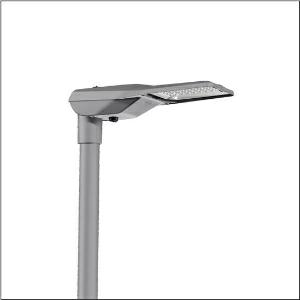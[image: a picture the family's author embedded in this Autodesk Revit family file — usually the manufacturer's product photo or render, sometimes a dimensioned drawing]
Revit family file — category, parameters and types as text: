
# Revit family: streetlight_sl_21_iq_mini___pl52_5xe2h31y08hb_fa04
name_source: partatom
category: Lighting Fixtures
units: mm (PartAtom-declared; Revit-internal decimal feet)

## family parameters
Cut with Voids When Loaded = No
Host = Face
Light Source = No
Part Type = Normal
Room Calculation Point = No
Round Connector Dimension = Use Diameter
Shared = No

## types (1)
- --- (1 x LED, 9580 lm, 71 W, 3000K)
    Apparent Load = 71 VA
    CIE Flux Codes = 27 59 98 100 100
    Color Rendering = 70
    Color Temperature = 3000K
    Default Elevation = 1800 mm
    Description = Streetlight SL 21 iQ mini, mast luminaire, primary light control with lens, of PMMA, primary optical cover: cover, of toughened safety glass, transparent, light distribution: PL52, light emission: direct distribution, primary light characteristic: asymmetric, installation type: post-top, side-entry, LED, High Power LED, rated luminous flux: 9.580lm, luminous efficacy: 135lm/W, light colour: 730, colour temperature: 3000K, control: presetting dimming logarithmic, Street-Remote, Auto-Match, Temp-Guard, Lumen-Switch, Night-Set, Smart-Wire, Light-Fading, Desk-Remote (wireless, voltage-free reading and setting of iQ features in the workshop via application-optimized NFC function/RFID function), optimised constant luminous flux control (CLO 2.0), mains connection: 220..240V, AC, 50/60Hz, start of lifetime: 71W, end of service life: 75W, reduction: 30W, luminaire housing, of diecast aluminium, powder-coated, Siteco® metallic grey (DB 702S), corrosivity category C5 mid according to DIN EN ISO 12944, please order mast flange separately, inclination adjustable: 0°, 5°, 10°, 15°, sealing non-destructively replaceable, multi-level sealing system, length: 628mm, width: 235mm, height: 110mm, mast flange for spigot size: 42mm (side-entry): 5XC10008XM4, 60/48mm (side-entry/post-top): 5XC10108XM2, 76/60mm (side-entry/post-top): 5XC10108XM1, Smart Interface below and above, protection rating (complete): IP66, insulation class (complete): insulation class II (safety insulation), certification: CE, ENEC, ENEC+, VDE, impact resistance: IK09, permissible operating ambient temperature for outdoor applications: -40..+50°C, standard-compliant lighting for roads and squares, packaging unit: 1 piece

Light Distribution: PL52
    Height = 110 mm
    Lamp = 1 x LED
    Lamp Light Flux = 9580 lm
    Lamp Power = 71 W
    Lamp count = 1
    Length = 625 mm
    Luminous efficacy = 135 lm/W
    Manufacturer = Siteco
    ModVariant = No
    Model = 5XE2H31Y08HB
    Number of Poles = 1
    OnlyDefault = Yes
    Power Factor = 1
    Product Name = Streetlight SL 21 iQ mini | PL52
    Product group = mast luminaire | pylon top
    ProductGroupID = 6100
    Protection Class = Protection class II
    Protection Degree = IP 66
    RLX_Detail_Level = 1
    RLX_Emergency_Light_Flux = 0 lm
    RLX_Emergency_Type = 0
    RLX_Emergency_Type_DB = No
    RlxData = <blob elided: 102113 chars, md5=1b4f9a65>
    Socket = socket
    Standby Power = 0 W
    System Light Flux = 9580 lm
    System Power = 71 W
    Type Comments = factory setting: luminous flux: 100 % | dim-lin: 254 | 716 mA
    Type Image = l_1003514.jpg
    URL = http://relux.com
    VarID = @adj_064109
    Voltage = 0 V
    Weight = 0.00 kg
    Width = 234 mm

## geometry (parser evidence)
native form markers: Blend x4, Sweep x11
no freeform markers — native parametric forms only
